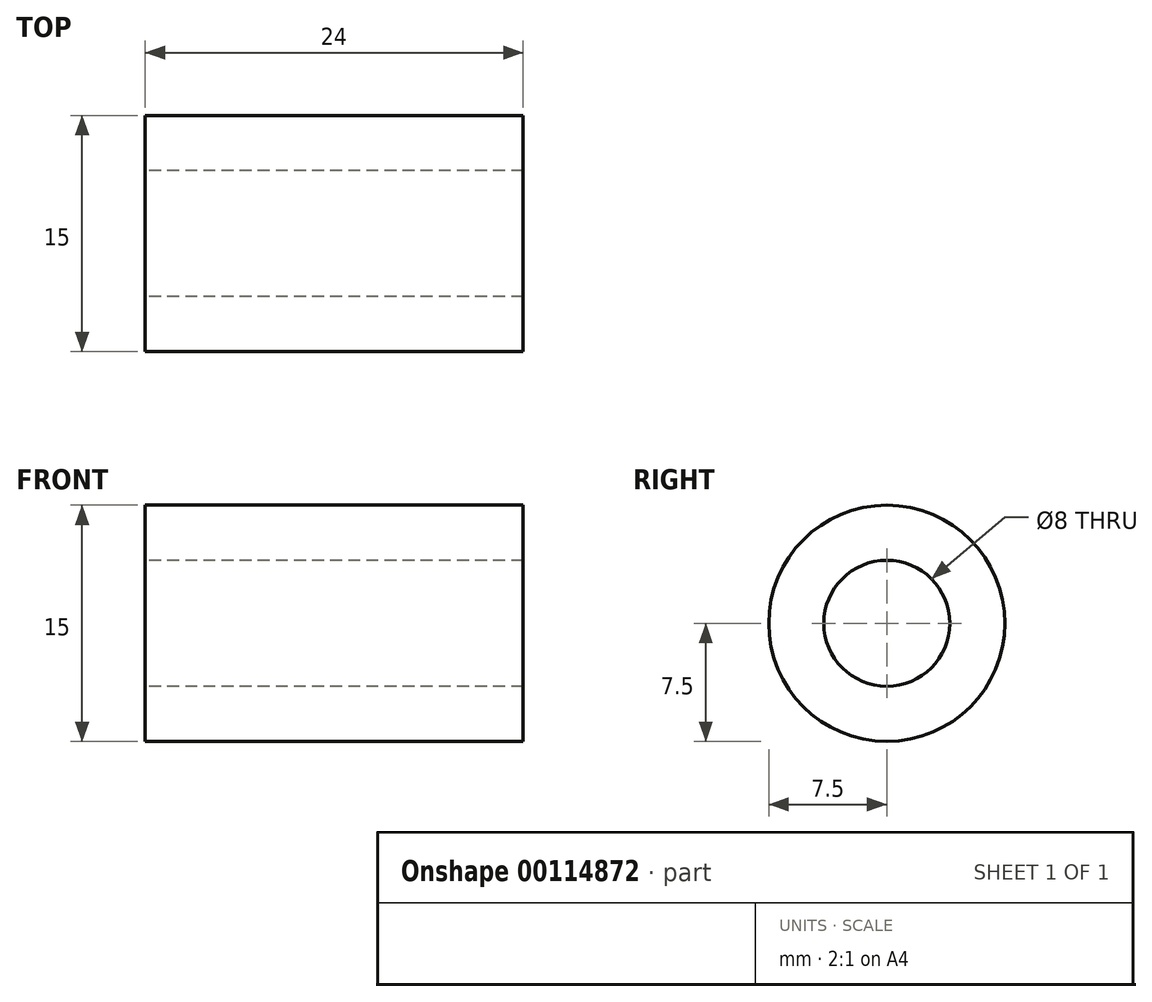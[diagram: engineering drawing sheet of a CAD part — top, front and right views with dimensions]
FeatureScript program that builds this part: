
annotation { "Feature Type Name" : "Feature", "Feature Type Description" : "" }
export const myFeature = defineFeature(function(context is Context, id is Id, definition is map)
    precondition{}
    {
        {
            var Q0;
            Q0=qCreatedBy(makeId("Right.planeOp"),FACE);
            var sketch = newSketch(context, id + "F0", { "sketchPlane" : qUnion([Q0])});
            skCircle(sketch, "E0", {"center": v(0, 0) * mm, "radius": 4 * mm});
            skCircle(sketch, "E1", {"center": v(0, 0) * mm, "radius": 7.5 * mm});
            skSolve(sketch);
        }
        {
            var Q0;
            Q0 = qSketchRegion(id + "F0", true);
            extrude(context, id + "F1", {"entities" : qUnion([Q0]), "depth" : 24 * mm});
        }
    });
